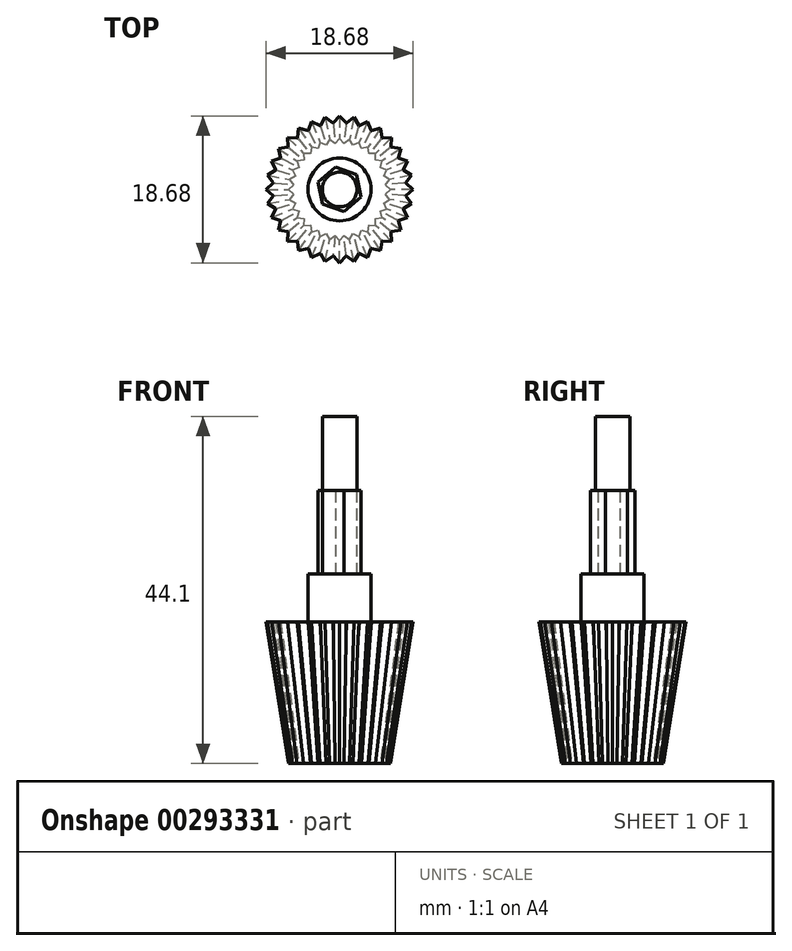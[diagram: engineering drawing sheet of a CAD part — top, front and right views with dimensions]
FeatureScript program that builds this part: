
annotation { "Feature Type Name" : "Feature", "Feature Type Description" : "" }
export const myFeature = defineFeature(function(context is Context, id is Id, definition is map)
    precondition{}
    {
        {
            var Q0;
            Q0=qCreatedBy(makeId("Top.planeOp"),FACE);
            var sketch = newSketch(context, id + "F0", { "sketchPlane" : qUnion([Q0])});
            skCircle(sketch, "E0", {"center": v(0, 0) * mm, "radius": 8.5 * mm});
            skSolve(sketch);
        }
        {
            var Q0;
            Q0=makeQuery(id+"F0.imprint","IMPRINT",FACE,{"disambiguationData":[TD([[makeQuery(id+"F0.imprint","IMPRINT",EDGE,{"derivedFrom":sQuery(id+"F0.wireOp",EDGE,"E0")}),1.0]])]});
            var Q1;
            Q1=sQuery(id+"F0.wireOp",EDGE,"E0");
            extrude(context, id + "F1", {"entities" : qUnion([Q0]), "surfaceEntities" : qUnion([Q1]), "oppositeDirection" : true, "depth" : 18 * mm, "hasDraft" : true, "draftAngle" : 9 * degree, "draftPullDirection" : true});
        }
        {
            var Q0;
            Q0=makeQuery(id+"F1.opExtrude","CAP_FACE",FACE,{"disambiguationData":[OSD([sQuery(id+"F0.wireOp",EDGE,"E0")])],"isStart":false});
            var sketch = newSketch(context, id + "F2", { "sketchPlane" : qUnion([Q0])});
            skLineSegment(sketch, "E1", {"start": v(-0.8, 5.6) * mm, "end": v(0, 6.47) * mm});
            skLineSegment(sketch, "E2", {"start": v(0, 6.47) * mm, "end": v(0.8, 5.6) * mm});
            skLineSegment(sketch, "E3", {"start": v(0.8, 5.6) * mm, "end": v(-0.8, 5.6) * mm});
            skSolve(sketch);
        }
        {
            var Q0;
            Q0=makeQuery(id+"F1.opExtrude","CAP_FACE",FACE,{"disambiguationData":[OSD([sQuery(id+"F0.wireOp",EDGE,"E0")])],"isStart":true});
            var sketch = newSketch(context, id + "F3", { "sketchPlane" : qUnion([Q0])});
            skLineSegment(sketch, "E4", {"start": v(-0.8, -8.46) * mm, "end": v(0, -9.34) * mm});
            skLineSegment(sketch, "E5", {"start": v(0, -9.34) * mm, "end": v(0.8, -8.46) * mm});
            skLineSegment(sketch, "E6", {"start": v(0.8, -8.46) * mm, "end": v(-0.8, -8.46) * mm});
            skSolve(sketch);
        }
        {
            var Q1;
            {var subQ0=sQuery(id+"F3.wireOp",EDGE,"E4");Q1=makeQuery(id+"F3.imprint","IMPRINT",FACE,{"disambiguationData":[TD([[makeQuery(id+"F3.imprint","IMPRINT",EDGE,{"derivedFrom":subQ0}),1.0]])]});}
            var Q2;
            {var subQ0=sQuery(id+"F2.wireOp",EDGE,"E1");Q2=makeQuery(id+"F2.imprint","IMPRINT",FACE,{"disambiguationData":[TD([[makeQuery(id+"F2.imprint","IMPRINT",EDGE,{"derivedFrom":subQ0}),-1.0]])]});}
            loft(context, id + "F4", {"operationType" : NewBodyOperationType.ADD, "sheetProfilesArray" : [{ "sheetProfileEntities" : qUnion([Q1]) }, { "sheetProfileEntities" : qUnion([Q2]) }]});
        }
        {
            var Q0;
            Q0=qCreatedBy(makeId("Front.planeOp"),FACE);
            var sketch = newSketch(context, id + "F5", { "sketchPlane" : qUnion([Q0])});
            skLineSegment(sketch, "E7", {"start": v(0, -24.65) * mm, "end": v(0, 8.96) * mm, "construction": true});
            skSolve(sketch);
        }
        {
            var Q0;
            {var subQ0=sQuery(id+"F3.wireOp",EDGE,"E4");var subQ5=sQuery(id+"F2.wireOp",EDGE,"E1");Q0=makeQuery(id+"F4.opLoft","SWEPT_BODY",BODY,{"disambiguationData":[OSD([makeQuery(id+"F2.imprint","IMPRINT",FACE,{"disambiguationData":[TD([[makeQuery(id+"F2.imprint","IMPRINT",EDGE,{"derivedFrom":subQ5}),-1.0]])]}),makeQuery(id+"F3.imprint","IMPRINT",FACE,{"disambiguationData":[TD([[makeQuery(id+"F3.imprint","IMPRINT",EDGE,{"derivedFrom":subQ0}),1.0]])]})])]});}
            var Q1;
            Q1=makeQuery(id+"F1.opExtrude","SWEPT_BODY",BODY,{"disambiguationData":[OSD([sQuery(id+"F0.wireOp",EDGE,"E0")])]});
            var Q2;
            Q2=sQuery(id+"F5.wireOp",EDGE,"E7");
            circularPattern(context, id + "F6", {"operationType" : NewBodyOperationType.ADD, "entities" : qUnion([Q0, Q1]), "axis" : qUnion([Q2]), "angle" : 360 * degree, "instanceCount" : 32, "equalSpace" : true});
        }
        {
            var Q0;
            {var subQ0=sQuery(id+"F3.wireOp",EDGE,"E4");var subQ3=sQuery(id+"F0.wireOp",EDGE,"E0");var subQ5=makeQuery(id+"F4.boolean.opBoolean","MERGE",FACE,{"derivedFrom":[makeQuery(id+"F1.opExtrude","CAP_FACE",FACE,{"disambiguationData":[OSD([subQ3])],"isStart":true}),makeQuery(id+"F4.opLoft","CAP_FACE",FACE,{"disambiguationData":[OSD([makeQuery(id+"F3.imprint","IMPRINT",FACE,{"disambiguationData":[TD([[makeQuery(id+"F3.imprint","IMPRINT",EDGE,{"derivedFrom":subQ0}),1.0]])]})])],"isStart":true})]});Q0=makeQuery(id+"F6.boolean.opBoolean","MERGE",FACE,{"derivedFrom":[subQ5,makeQuery(id+"F6.opPattern","COPY",FACE,{"derivedFrom":subQ5,"instanceName":"1"}),makeQuery(id+"F6.opPattern","COPY",FACE,{"derivedFrom":subQ5,"instanceName":"2"}),makeQuery(id+"F6.opPattern","COPY",FACE,{"derivedFrom":subQ5,"instanceName":"3"}),makeQuery(id+"F6.opPattern","COPY",FACE,{"derivedFrom":subQ5,"instanceName":"4"}),makeQuery(id+"F6.opPattern","COPY",FACE,{"derivedFrom":subQ5,"instanceName":"5"}),makeQuery(id+"F6.opPattern","COPY",FACE,{"derivedFrom":subQ5,"instanceName":"6"}),makeQuery(id+"F6.opPattern","COPY",FACE,{"derivedFrom":subQ5,"instanceName":"7"}),makeQuery(id+"F6.opPattern","COPY",FACE,{"derivedFrom":subQ5,"instanceName":"8"}),makeQuery(id+"F6.opPattern","COPY",FACE,{"derivedFrom":subQ5,"instanceName":"9"}),makeQuery(id+"F6.opPattern","COPY",FACE,{"derivedFrom":subQ5,"instanceName":"10"}),makeQuery(id+"F6.opPattern","COPY",FACE,{"derivedFrom":subQ5,"instanceName":"11"}),makeQuery(id+"F6.opPattern","COPY",FACE,{"derivedFrom":subQ5,"instanceName":"12"}),makeQuery(id+"F6.opPattern","COPY",FACE,{"derivedFrom":subQ5,"instanceName":"13"}),makeQuery(id+"F6.opPattern","COPY",FACE,{"derivedFrom":subQ5,"instanceName":"14"}),makeQuery(id+"F6.opPattern","COPY",FACE,{"derivedFrom":subQ5,"instanceName":"15"}),makeQuery(id+"F6.opPattern","COPY",FACE,{"derivedFrom":subQ5,"instanceName":"16"}),makeQuery(id+"F6.opPattern","COPY",FACE,{"derivedFrom":subQ5,"instanceName":"17"}),makeQuery(id+"F6.opPattern","COPY",FACE,{"derivedFrom":subQ5,"instanceName":"18"}),makeQuery(id+"F6.opPattern","COPY",FACE,{"derivedFrom":subQ5,"instanceName":"19"}),makeQuery(id+"F6.opPattern","COPY",FACE,{"derivedFrom":subQ5,"instanceName":"20"}),makeQuery(id+"F6.opPattern","COPY",FACE,{"derivedFrom":subQ5,"instanceName":"21"}),makeQuery(id+"F6.opPattern","COPY",FACE,{"derivedFrom":subQ5,"instanceName":"22"}),makeQuery(id+"F6.opPattern","COPY",FACE,{"derivedFrom":subQ5,"instanceName":"23"}),makeQuery(id+"F6.opPattern","COPY",FACE,{"derivedFrom":subQ5,"instanceName":"24"}),makeQuery(id+"F6.opPattern","COPY",FACE,{"derivedFrom":subQ5,"instanceName":"25"}),makeQuery(id+"F6.opPattern","COPY",FACE,{"derivedFrom":subQ5,"instanceName":"26"}),makeQuery(id+"F6.opPattern","COPY",FACE,{"derivedFrom":subQ5,"instanceName":"27"}),makeQuery(id+"F6.opPattern","COPY",FACE,{"derivedFrom":subQ5,"instanceName":"28"}),makeQuery(id+"F6.opPattern","COPY",FACE,{"derivedFrom":subQ5,"instanceName":"29"}),makeQuery(id+"F6.opPattern","COPY",FACE,{"derivedFrom":subQ5,"instanceName":"30"}),makeQuery(id+"F6.opPattern","COPY",FACE,{"derivedFrom":subQ5,"instanceName":"31"})]});}
            var sketch = newSketch(context, id + "F7", { "sketchPlane" : qUnion([Q0])});
            skCircle(sketch, "E8", {"center": v(0, 0) * mm, "radius": 4 * mm});
            skSolve(sketch);
        }
        {
            var Q0;
            Q0=makeQuery(id+"F7.imprint","IMPRINT",FACE,{"disambiguationData":[TD([[makeQuery(id+"F7.imprint","IMPRINT",EDGE,{"derivedFrom":sQuery(id+"F7.wireOp",EDGE,"E8")}),1.0]])]});
            extrude(context, id + "F8", {"entities" : qUnion([Q0]), "operationType" : NewBodyOperationType.ADD, "depth" : 6.1 * mm});
        }
        {
            var Q0;
            Q0=makeQuery(id+"F8.opExtrude","CAP_FACE",FACE,{"disambiguationData":[OSD([sQuery(id+"F7.wireOp",EDGE,"E8")])],"isStart":false});
            var sketch = newSketch(context, id + "F9", { "sketchPlane" : qUnion([Q0])});
            skCircle(sketch, "E9.cCircle", {"center": v(0, 0) * mm, "radius": 2.49 * mm, "construction": true});
            skLineSegment(sketch, "E9.0", {"start": v(-2.71, 0.94) * mm, "end": v(-0.54, 2.82) * mm});
            skLineSegment(sketch, "E9.1", {"start": v(-0.54, 2.82) * mm, "end": v(2.17, 1.88) * mm});
            skLineSegment(sketch, "E9.2", {"start": v(2.17, 1.88) * mm, "end": v(2.71, -0.94) * mm});
            skLineSegment(sketch, "E9.3", {"start": v(2.71, -0.94) * mm, "end": v(0.54, -2.82) * mm});
            skLineSegment(sketch, "E9.4", {"start": v(0.54, -2.82) * mm, "end": v(-2.17, -1.88) * mm});
            skLineSegment(sketch, "E9.5", {"start": v(-2.17, -1.88) * mm, "end": v(-2.71, 0.94) * mm});
            skPoint(sketch, "E9.0.midPoint", {"position": v(-1.63, 1.88) * mm});
            skSolve(sketch);
        }
        {
            var Q0;
            Q0=makeQuery(id+"F9.imprint","IMPRINT",FACE,{"disambiguationData":[TD([[makeQuery(id+"F9.imprint","IMPRINT",EDGE,{"derivedFrom":sQuery(id+"F9.wireOp",EDGE,"E9.0")}),-1.0]])]});
            extrude(context, id + "F10", {"entities" : qUnion([Q0]), "operationType" : NewBodyOperationType.ADD, "depth" : 10.6 * mm});
        }
        {
            var Q0;
            Q0=makeQuery(id+"F10.opExtrude","CAP_FACE",FACE,{"disambiguationData":[OSD([sQuery(id+"F9.wireOp",EDGE,"E9.0"),sQuery(id+"F9.wireOp",EDGE,"E9.1"),sQuery(id+"F9.wireOp",EDGE,"E9.2"),sQuery(id+"F9.wireOp",EDGE,"E9.3"),sQuery(id+"F9.wireOp",EDGE,"E9.4"),sQuery(id+"F9.wireOp",EDGE,"E9.5")])],"isStart":false});
            var sketch = newSketch(context, id + "F11", { "sketchPlane" : qUnion([Q0])});
            skCircle(sketch, "E10", {"center": v(0, 0) * mm, "radius": 2.2 * mm});
            skSolve(sketch);
        }
        {
            var Q0;
            Q0=makeQuery(id+"F11.imprint","IMPRINT",FACE,{"disambiguationData":[TD([[makeQuery(id+"F11.imprint","IMPRINT",EDGE,{"derivedFrom":sQuery(id+"F11.wireOp",EDGE,"E10")}),1.0]])]});
            extrude(context, id + "F12", {"entities" : qUnion([Q0]), "operationType" : NewBodyOperationType.ADD, "depth" : 9.4 * mm});
        }
    });
